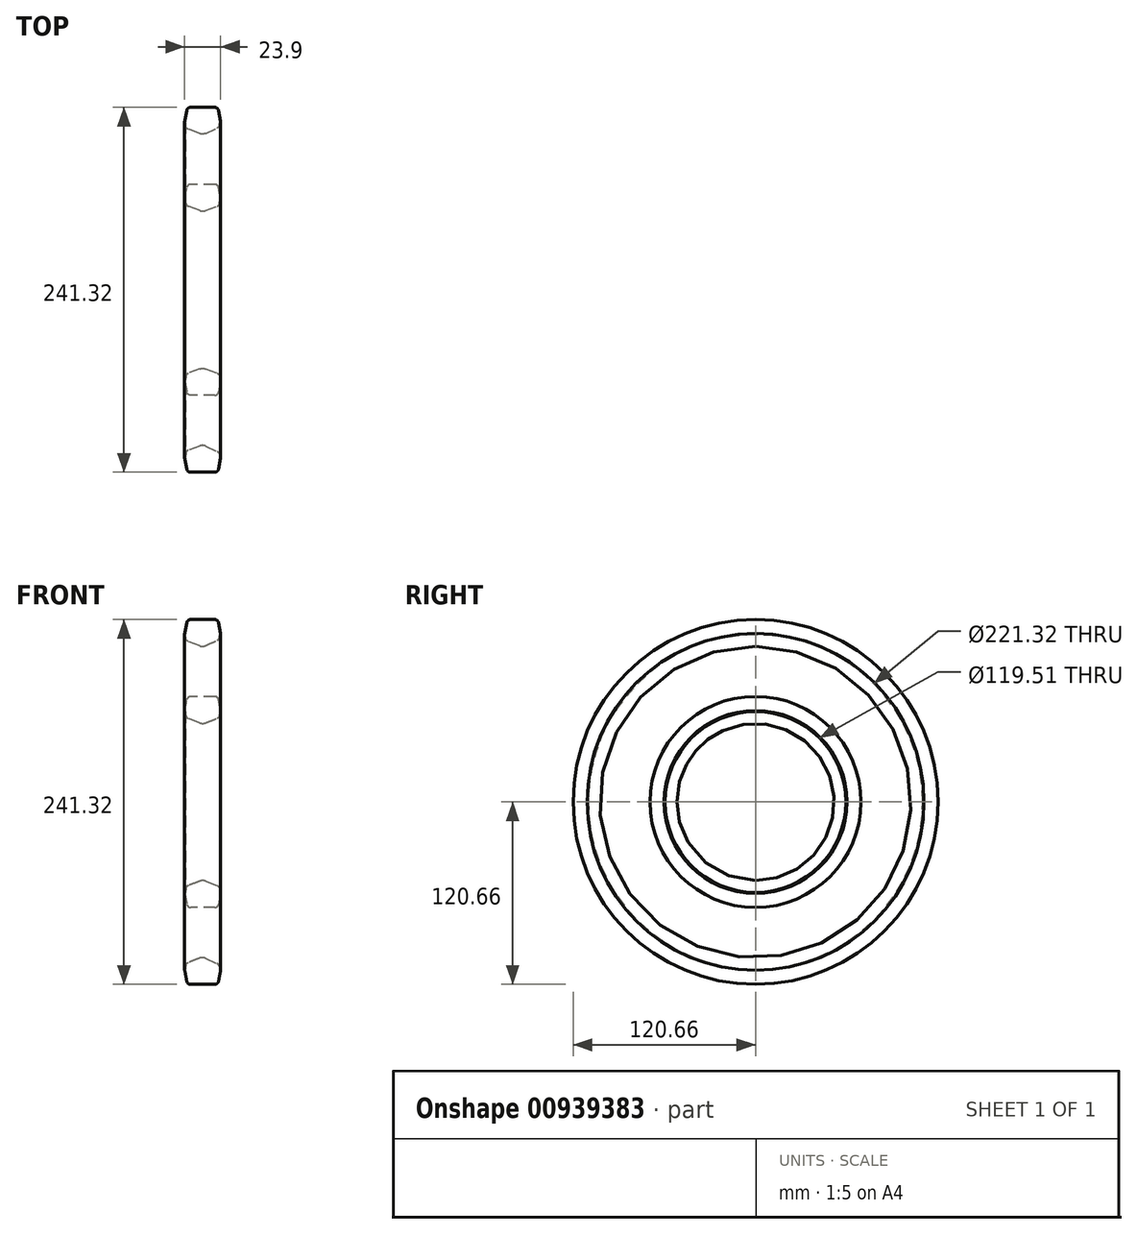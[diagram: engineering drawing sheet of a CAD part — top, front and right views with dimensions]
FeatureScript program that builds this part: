
annotation { "Feature Type Name" : "Feature", "Feature Type Description" : "" }
export const myFeature = defineFeature(function(context is Context, id is Id, definition is map)
    precondition{}
    {
        {
            var Q0;
            Q0=qCreatedBy(makeId("Front.planeOp"),FACE);
            var sketch = newSketch(context, id + "F0", { "sketchPlane" : qUnion([Q0])});
            skLineSegment(sketch, "E0", {"start": v(0, 0) * mm, "end": v(0, 102.54) * mm});
            skLineSegment(sketch, "E1", {"start": v(11.39, 111.4) * mm, "end": v(11.85, 111.4) * mm});
            skLineSegment(sketch, "E2", {"start": v(-0.01, 120.66) * mm, "end": v(10.09, 120.66) * mm});
            skLineSegment(sketch, "E3", {"start": v(10.09, 120.66) * mm, "end": v(11.85, 111.4) * mm});
            skLineSegment(sketch, "E4", {"start": v(10.86, 107.46) * mm, "end": v(11.39, 111.4) * mm});
            skLineSegment(sketch, "E5", {"start": v(11.39, 111.4) * mm, "end": v(10.86, 107.46) * mm});
            skLineSegment(sketch, "E6", {"start": v(-0.01, 102.54) * mm, "end": v(10.86, 107.46) * mm});
            skLineSegment(sketch, "E7", {"start": v(11.85, 111.4) * mm, "end": v(11.39, 111.4) * mm});
            skLineSegment(sketch, "E8", {"start": v(-0.01, 120.66) * mm, "end": v(-10.11, 120.66) * mm});
            skLineSegment(sketch, "E9", {"start": v(-11.54, 110.66) * mm, "end": v(-12.01, 110.66) * mm});
            skLineSegment(sketch, "E10", {"start": v(-11.01, 106.72) * mm, "end": v(-0.01, 102.54) * mm});
            skLineSegment(sketch, "E11", {"start": v(-11.54, 110.66) * mm, "end": v(-11.01, 106.72) * mm});
            skLineSegment(sketch, "E12", {"start": v(-12.01, 110.66) * mm, "end": v(-10.11, 120.66) * mm});
            skLineSegment(sketch, "E13", {"start": v(0, 0) * mm, "end": v(-12.6, 0) * mm});
            skSolve(sketch);
        }
        {
            var Q0;
            Q0=qCreatedBy(makeId("Front.planeOp"),FACE);
            var sketch = newSketch(context, id + "F1", { "sketchPlane" : qUnion([Q0])});
            skLineSegment(sketch, "E14", {"start": v(0, 0) * mm, "end": v(0, 69.85) * mm});
            skLineSegment(sketch, "E15", {"start": v(11.56, 59.75) * mm, "end": v(11.89, 60.5) * mm});
            skLineSegment(sketch, "E16", {"start": v(0.03, 69.75) * mm, "end": v(10.13, 69.75) * mm});
            skLineSegment(sketch, "E17", {"start": v(10.13, 69.75) * mm, "end": v(11.89, 60.5) * mm});
            skLineSegment(sketch, "E18", {"start": v(11.03, 55.81) * mm, "end": v(11.56, 59.75) * mm});
            skLineSegment(sketch, "E19", {"start": v(11.56, 59.75) * mm, "end": v(11.03, 55.81) * mm});
            skLineSegment(sketch, "E20", {"start": v(0.03, 51.63) * mm, "end": v(11.03, 55.81) * mm});
            skLineSegment(sketch, "E21", {"start": v(11.89, 60.5) * mm, "end": v(11.56, 59.75) * mm});
            skLineSegment(sketch, "E22", {"start": v(0.03, 69.75) * mm, "end": v(-10.07, 69.75) * mm});
            skLineSegment(sketch, "E23", {"start": v(-11.5, 59.75) * mm, "end": v(-11.97, 59.75) * mm});
            skLineSegment(sketch, "E24", {"start": v(-10.97, 55.81) * mm, "end": v(0.03, 51.63) * mm});
            skLineSegment(sketch, "E25", {"start": v(-11.5, 59.75) * mm, "end": v(-10.97, 55.81) * mm});
            skLineSegment(sketch, "E26", {"start": v(-11.97, 59.75) * mm, "end": v(-10.07, 69.75) * mm});
            skLineSegment(sketch, "E27", {"start": v(0, 0) * mm, "end": v(11.47, 0) * mm});
            skSolve(sketch);
        }
        {
            var Q0;
            Q0 = qSketchRegion(id + "F0", true);
            var Q1;
            Q1=sQuery(id+"F0.wireOp",EDGE,"E13");
            revolve(context, id + "F2", {"surfaceOperationType" : NewSurfaceOperationType.NEW, "entities" : qUnion([Q0]), "axis" : qUnion([Q1]), "revolveType" : RevolveType.FULL});
        }
        {
            var Q0;
            Q0 = qSketchRegion(id + "F1", true);
            var Q1;
            Q1=sQuery(id+"F1.wireOp",EDGE,"E27");
            revolve(context, id + "F3", {"surfaceOperationType" : NewSurfaceOperationType.NEW, "entities" : qUnion([Q0]), "axis" : qUnion([Q1]), "revolveType" : RevolveType.FULL});
        }
        {
            var Q0;
            Q0=makeQuery(id+"F3.opRevolve","SWEPT_EDGE",EDGE,{"disambiguationData":[OSD([sQuery(id+"F1.wireOp",EDGE,"E20"),sQuery(id+"F1.wireOp",EDGE,"E24")])]});
            var Q1;
            Q1=makeQuery(id+"F2.opRevolve","SWEPT_EDGE",EDGE,{"disambiguationData":[OSD([sQuery(id+"F0.wireOp",EDGE,"E6"),sQuery(id+"F0.wireOp",EDGE,"E10")])]});
            fillet(context, id + "F4", {"entities" : qUnion([Q0, Q1]), "radius" : 5.08 * mm, "tangentPropagation" : true, "allowEdgeOverflow" : false});
        }
        {
            var Q0;
            Q0=makeQuery(id+"F2.opRevolve","SWEPT_EDGE",EDGE,{"disambiguationData":[OSD([sQuery(id+"F0.wireOp",EDGE,"E8"),sQuery(id+"F0.wireOp",EDGE,"E12")])]});
            var Q1;
            Q1=makeQuery(id+"F2.opRevolve","SWEPT_EDGE",EDGE,{"disambiguationData":[OSD([sQuery(id+"F0.wireOp",EDGE,"E2"),sQuery(id+"F0.wireOp",EDGE,"E3")])]});
            var Q2;
            Q2=makeQuery(id+"F3.opRevolve","SWEPT_EDGE",EDGE,{"disambiguationData":[OSD([sQuery(id+"F1.wireOp",EDGE,"E22"),sQuery(id+"F1.wireOp",EDGE,"E26")])]});
            var Q3;
            Q3=makeQuery(id+"F3.opRevolve","SWEPT_EDGE",EDGE,{"disambiguationData":[OSD([sQuery(id+"F1.wireOp",EDGE,"E16"),sQuery(id+"F1.wireOp",EDGE,"E17")])]});
            var Q4;
            Q4=makeQuery(id+"F2.opRevolve","SWEPT_EDGE",EDGE,{"disambiguationData":[OSD([sQuery(id+"F0.wireOp",EDGE,"E10"),sQuery(id+"F0.wireOp",EDGE,"E11")])]});
            var Q5;
            Q5=makeQuery(id+"F3.opRevolve","SWEPT_EDGE",EDGE,{"disambiguationData":[OSD([sQuery(id+"F1.wireOp",EDGE,"E24"),sQuery(id+"F1.wireOp",EDGE,"E25")])]});
            var Q6;
            Q6=makeQuery(id+"F3.opRevolve","SWEPT_EDGE",EDGE,{"disambiguationData":[OSD([sQuery(id+"F1.wireOp",EDGE,"E19"),sQuery(id+"F1.wireOp",EDGE,"E20")])]});
            var Q7;
            Q7=makeQuery(id+"F2.opRevolve","SWEPT_EDGE",EDGE,{"disambiguationData":[OSD([sQuery(id+"F0.wireOp",EDGE,"E5"),sQuery(id+"F0.wireOp",EDGE,"E6")])]});
            fillet(context, id + "F5", {"entities" : qUnion([Q0, Q1, Q2, Q3, Q4, Q5, Q6, Q7]), "radius" : 2.54 * mm, "tangentPropagation" : true, "allowEdgeOverflow" : false});
        }
    });
